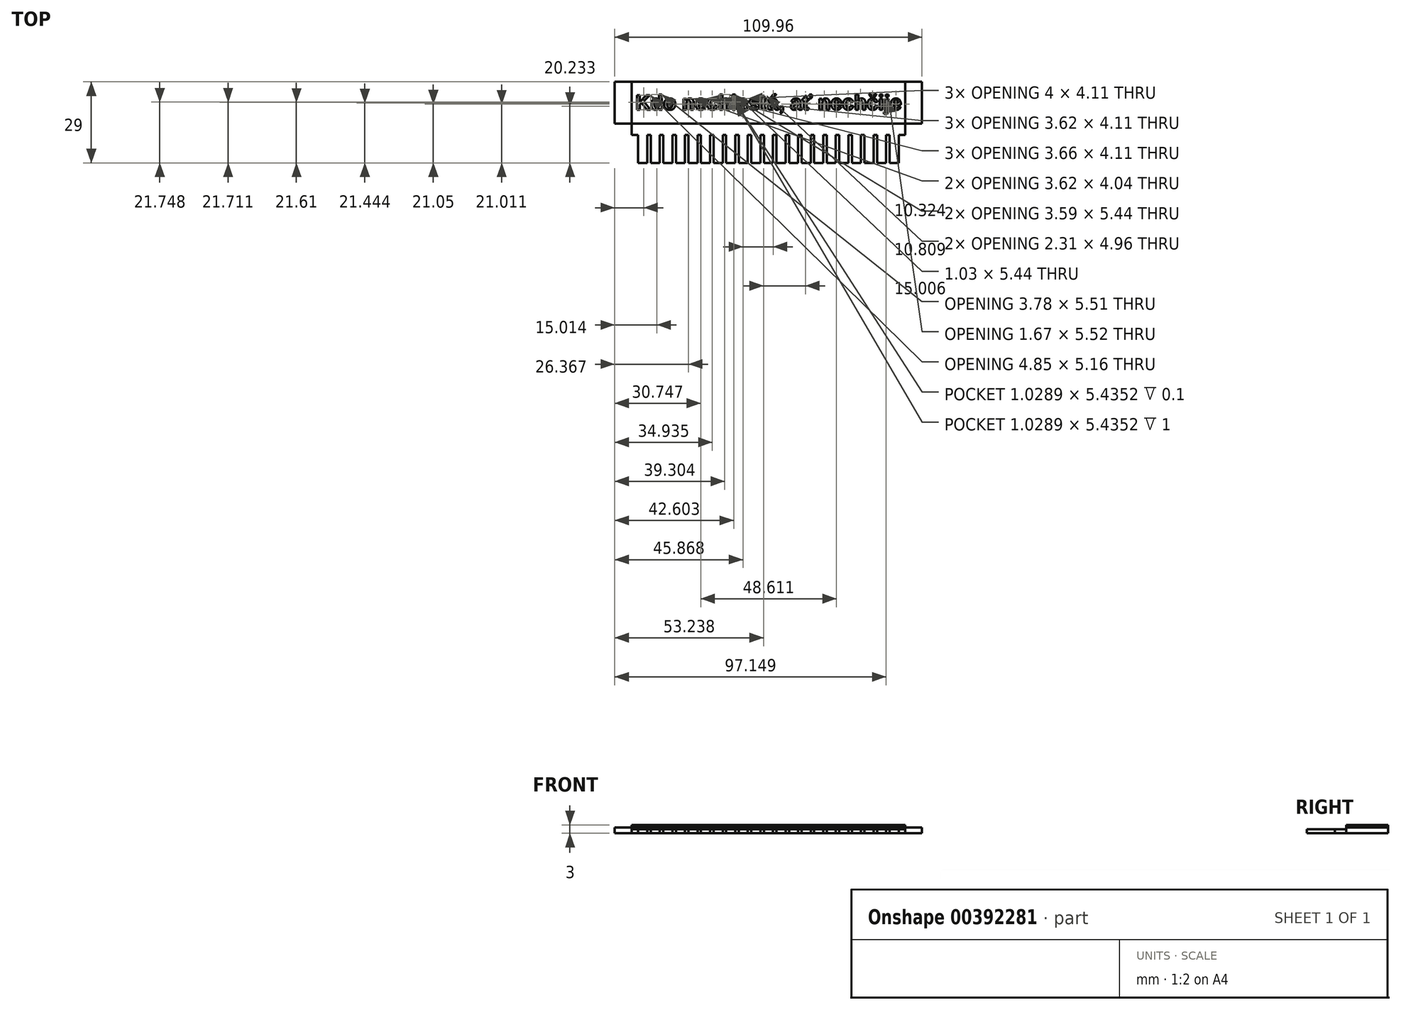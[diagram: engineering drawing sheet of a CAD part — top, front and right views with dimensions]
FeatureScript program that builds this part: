
annotation { "Feature Type Name" : "Feature", "Feature Type Description" : "" }
export const myFeature = defineFeature(function(context is Context, id is Id, definition is map)
    precondition{}
    {
        {
            var Q0;
            Q0=qCreatedBy(makeId("Top.planeOp"),FACE);
            var sketch = newSketch(context, id + "F0", { "sketchPlane" : qUnion([Q0])});
            skLineSegment(sketch, "E0.bottom", {"start": v(45.28, -13.18) * mm, "end": v(42.03, -13.18) * mm});
            skLineSegment(sketch, "E1.right", {"start": v(-47.97, -13.18) * mm, "end": v(-47.97, -3.18) * mm});
            skLineSegment(sketch, "E2.bottom", {"start": v(-47.97, -13.18) * mm, "end": v(-44.72, -13.18) * mm});
            skLineSegment(sketch, "E2.right", {"start": v(-44.72, -13.18) * mm, "end": v(-44.72, -3.18) * mm});
            skLineSegment(sketch, "E3.top", {"start": v(-44.72, -3.18) * mm, "end": v(-43.47, -3.18) * mm});
            skLineSegment(sketch, "E3.right", {"start": v(-43.47, -13.18) * mm, "end": v(-43.47, -3.18) * mm});
            skLineSegment(sketch, "E4.bottom", {"start": v(-43.47, -13.18) * mm, "end": v(-40.22, -13.18) * mm});
            skLineSegment(sketch, "E4.right", {"start": v(-40.22, -13.18) * mm, "end": v(-40.22, -3.18) * mm});
            skLineSegment(sketch, "E5.top", {"start": v(-40.22, -3.18) * mm, "end": v(-38.97, -3.18) * mm});
            skLineSegment(sketch, "E5.right", {"start": v(-38.97, -13.18) * mm, "end": v(-38.97, -3.18) * mm});
            skLineSegment(sketch, "E6.bottom", {"start": v(-38.97, -13.18) * mm, "end": v(-35.72, -13.18) * mm});
            skLineSegment(sketch, "E6.right", {"start": v(-35.72, -13.18) * mm, "end": v(-35.72, -3.18) * mm});
            skLineSegment(sketch, "E7.top", {"start": v(-35.72, -3.18) * mm, "end": v(-34.47, -3.18) * mm});
            skLineSegment(sketch, "E7.right", {"start": v(-34.47, -13.18) * mm, "end": v(-34.47, -3.18) * mm});
            skLineSegment(sketch, "E8.bottom", {"start": v(-34.47, -13.18) * mm, "end": v(-31.22, -13.18) * mm});
            skLineSegment(sketch, "E8.right", {"start": v(-31.22, -13.18) * mm, "end": v(-31.22, -3.18) * mm});
            skLineSegment(sketch, "E9.top", {"start": v(-31.22, -3.18) * mm, "end": v(-29.97, -3.18) * mm});
            skLineSegment(sketch, "E9.right", {"start": v(-29.97, -13.18) * mm, "end": v(-29.97, -3.18) * mm});
            skLineSegment(sketch, "E10.bottom", {"start": v(-29.97, -13.18) * mm, "end": v(-26.72, -13.18) * mm});
            skLineSegment(sketch, "E10.right", {"start": v(-26.72, -13.18) * mm, "end": v(-26.72, -3.18) * mm});
            skLineSegment(sketch, "E11.top", {"start": v(-26.72, -3.18) * mm, "end": v(-25.47, -3.18) * mm});
            skLineSegment(sketch, "E11.right", {"start": v(-25.47, -13.18) * mm, "end": v(-25.47, -3.18) * mm});
            skLineSegment(sketch, "E12.bottom", {"start": v(-25.47, -13.18) * mm, "end": v(-22.22, -13.18) * mm});
            skLineSegment(sketch, "E12.right", {"start": v(-22.22, -13.18) * mm, "end": v(-22.22, -3.18) * mm});
            skLineSegment(sketch, "E13.right", {"start": v(-20.97, -13.18) * mm, "end": v(-20.97, -3.18) * mm});
            skLineSegment(sketch, "E14.bottom", {"start": v(-20.97, -13.18) * mm, "end": v(-17.72, -13.18) * mm});
            skLineSegment(sketch, "E14.right", {"start": v(-17.72, -13.18) * mm, "end": v(-17.72, -3.18) * mm});
            skLineSegment(sketch, "E15.top", {"start": v(-17.72, -3.18) * mm, "end": v(-16.47, -3.18) * mm});
            skLineSegment(sketch, "E15.right", {"start": v(-16.47, -13.18) * mm, "end": v(-16.47, -3.18) * mm});
            skLineSegment(sketch, "E16.bottom", {"start": v(-16.47, -13.18) * mm, "end": v(-13.22, -13.18) * mm});
            skLineSegment(sketch, "E16.right", {"start": v(-13.22, -13.18) * mm, "end": v(-13.22, -3.18) * mm});
            skLineSegment(sketch, "E17.top", {"start": v(-13.22, -3.18) * mm, "end": v(-11.97, -3.18) * mm});
            skLineSegment(sketch, "E17.right", {"start": v(-11.97, -13.18) * mm, "end": v(-11.97, -3.18) * mm});
            skLineSegment(sketch, "E18.bottom", {"start": v(-11.97, -13.18) * mm, "end": v(-8.72, -13.18) * mm});
            skLineSegment(sketch, "E18.right", {"start": v(-8.72, -13.18) * mm, "end": v(-8.72, -3.18) * mm});
            skLineSegment(sketch, "E19.top", {"start": v(-8.72, -3.18) * mm, "end": v(-7.47, -3.18) * mm});
            skLineSegment(sketch, "E19.right", {"start": v(-7.47, -13.18) * mm, "end": v(-7.47, -3.18) * mm});
            skLineSegment(sketch, "E20.bottom", {"start": v(-7.47, -13.18) * mm, "end": v(-4.22, -13.18) * mm});
            skLineSegment(sketch, "E20.right", {"start": v(-4.22, -13.18) * mm, "end": v(-4.22, -3.18) * mm});
            skLineSegment(sketch, "E21.top", {"start": v(-4.22, -3.18) * mm, "end": v(-2.97, -3.18) * mm});
            skLineSegment(sketch, "E21.right", {"start": v(-2.97, -13.18) * mm, "end": v(-2.97, -3.18) * mm});
            skLineSegment(sketch, "E22.bottom", {"start": v(-2.97, -13.18) * mm, "end": v(0.28, -13.18) * mm});
            skLineSegment(sketch, "E22.right", {"start": v(0.28, -13.18) * mm, "end": v(0.28, -3.18) * mm});
            skLineSegment(sketch, "E23.top", {"start": v(0.28, -3.18) * mm, "end": v(1.53, -3.18) * mm});
            skLineSegment(sketch, "E23.right", {"start": v(1.53, -13.18) * mm, "end": v(1.53, -3.18) * mm});
            skLineSegment(sketch, "E24.bottom", {"start": v(1.53, -13.18) * mm, "end": v(4.78, -13.18) * mm});
            skLineSegment(sketch, "E24.right", {"start": v(4.78, -13.18) * mm, "end": v(4.78, -3.18) * mm});
            skLineSegment(sketch, "E25.top", {"start": v(4.78, -3.18) * mm, "end": v(6.03, -3.18) * mm});
            skLineSegment(sketch, "E25.right", {"start": v(6.03, -13.18) * mm, "end": v(6.03, -3.18) * mm});
            skLineSegment(sketch, "E26.bottom", {"start": v(6.03, -13.18) * mm, "end": v(9.28, -13.18) * mm});
            skLineSegment(sketch, "E26.right", {"start": v(9.28, -13.18) * mm, "end": v(9.28, -3.18) * mm});
            skLineSegment(sketch, "E27.top", {"start": v(9.28, -3.18) * mm, "end": v(10.53, -3.18) * mm});
            skLineSegment(sketch, "E27.right", {"start": v(10.53, -13.18) * mm, "end": v(10.53, -3.18) * mm});
            skLineSegment(sketch, "E28.bottom", {"start": v(10.53, -13.18) * mm, "end": v(13.78, -13.18) * mm});
            skLineSegment(sketch, "E28.right", {"start": v(13.78, -13.18) * mm, "end": v(13.78, -3.18) * mm});
            skLineSegment(sketch, "E29.top", {"start": v(13.78, -3.18) * mm, "end": v(15.03, -3.18) * mm});
            skLineSegment(sketch, "E29.right", {"start": v(15.03, -13.18) * mm, "end": v(15.03, -3.18) * mm});
            skLineSegment(sketch, "E30.bottom", {"start": v(15.03, -13.18) * mm, "end": v(18.28, -13.18) * mm});
            skLineSegment(sketch, "E30.right", {"start": v(18.28, -13.18) * mm, "end": v(18.28, -3.18) * mm});
            skLineSegment(sketch, "E31.top", {"start": v(18.28, -3.18) * mm, "end": v(19.53, -3.18) * mm});
            skLineSegment(sketch, "E31.right", {"start": v(19.53, -13.18) * mm, "end": v(19.53, -3.18) * mm});
            skLineSegment(sketch, "E32.bottom", {"start": v(19.53, -13.18) * mm, "end": v(22.78, -13.18) * mm});
            skLineSegment(sketch, "E32.right", {"start": v(22.78, -13.18) * mm, "end": v(22.78, -3.18) * mm});
            skLineSegment(sketch, "E33.top", {"start": v(22.78, -3.18) * mm, "end": v(24.03, -3.18) * mm});
            skLineSegment(sketch, "E33.right", {"start": v(24.03, -13.18) * mm, "end": v(24.03, -3.18) * mm});
            skLineSegment(sketch, "E34.bottom", {"start": v(24.03, -13.18) * mm, "end": v(27.28, -13.18) * mm});
            skLineSegment(sketch, "E34.right", {"start": v(27.28, -13.18) * mm, "end": v(27.28, -3.18) * mm});
            skLineSegment(sketch, "E35.top", {"start": v(27.28, -3.18) * mm, "end": v(28.53, -3.18) * mm});
            skLineSegment(sketch, "E35.right", {"start": v(28.53, -13.18) * mm, "end": v(28.53, -3.18) * mm});
            skLineSegment(sketch, "E36.bottom", {"start": v(28.53, -13.18) * mm, "end": v(31.78, -13.18) * mm});
            skLineSegment(sketch, "E36.right", {"start": v(31.78, -13.18) * mm, "end": v(31.78, -3.18) * mm});
            skLineSegment(sketch, "E37.top", {"start": v(31.78, -3.18) * mm, "end": v(33.03, -3.18) * mm});
            skLineSegment(sketch, "E37.right", {"start": v(33.03, -13.18) * mm, "end": v(33.03, -3.18) * mm});
            skLineSegment(sketch, "E38.bottom", {"start": v(33.03, -13.18) * mm, "end": v(36.28, -13.18) * mm});
            skLineSegment(sketch, "E38.right", {"start": v(36.28, -13.18) * mm, "end": v(36.28, -3.18) * mm});
            skLineSegment(sketch, "E39.top", {"start": v(36.28, -3.18) * mm, "end": v(37.53, -3.18) * mm});
            skLineSegment(sketch, "E39.right", {"start": v(37.53, -13.18) * mm, "end": v(37.53, -3.18) * mm});
            skLineSegment(sketch, "E40.bottom", {"start": v(37.53, -13.18) * mm, "end": v(40.78, -13.18) * mm});
            skLineSegment(sketch, "E40.right", {"start": v(40.78, -13.18) * mm, "end": v(40.78, -3.18) * mm});
            skLineSegment(sketch, "E41.bottom", {"start": v(42.03, -13.18) * mm, "end": v(45.28, -13.18) * mm});
            skLineSegment(sketch, "E41.left", {"start": v(42.03, -13.18) * mm, "end": v(42.03, -3.18) * mm});
            skLineSegment(sketch, "E42.left", {"start": v(45.28, -13.18) * mm, "end": v(45.28, -3.18) * mm});
            skLineSegment(sketch, "E43.trimOffspring", {"start": v(36.28, -13.18) * mm, "end": v(33.03, -13.18) * mm});
            skLineSegment(sketch, "E44.trimOffspring", {"start": v(31.78, -13.18) * mm, "end": v(28.53, -13.18) * mm});
            skLineSegment(sketch, "E45.trimOffspring", {"start": v(27.28, -13.18) * mm, "end": v(24.03, -13.18) * mm});
            skLineSegment(sketch, "E46.trimOffspring", {"start": v(22.78, -13.18) * mm, "end": v(19.53, -13.18) * mm});
            skLineSegment(sketch, "E47.trimOffspring", {"start": v(18.28, -13.18) * mm, "end": v(15.03, -13.18) * mm});
            skLineSegment(sketch, "E48.trimOffspring", {"start": v(13.78, -13.18) * mm, "end": v(10.53, -13.18) * mm});
            skLineSegment(sketch, "E49.trimOffspring", {"start": v(9.28, -13.18) * mm, "end": v(6.03, -13.18) * mm});
            skLineSegment(sketch, "E50.trimOffspring", {"start": v(4.78, -13.18) * mm, "end": v(1.53, -13.18) * mm});
            skLineSegment(sketch, "E51.trimOffspring", {"start": v(0.28, -13.18) * mm, "end": v(-2.97, -13.18) * mm});
            skLineSegment(sketch, "E52.trimOffspring", {"start": v(-4.22, -13.18) * mm, "end": v(-7.47, -13.18) * mm});
            skLineSegment(sketch, "E53.trimOffspring", {"start": v(-8.72, -13.18) * mm, "end": v(-11.97, -13.18) * mm});
            skLineSegment(sketch, "E54.trimOffspring", {"start": v(-13.22, -13.18) * mm, "end": v(-16.47, -13.18) * mm});
            skLineSegment(sketch, "E55.trimOffspring", {"start": v(-22.22, -13.18) * mm, "end": v(-25.47, -13.18) * mm});
            skLineSegment(sketch, "E56.trimOffspring", {"start": v(-26.72, -13.18) * mm, "end": v(-29.97, -13.18) * mm});
            skLineSegment(sketch, "E57.trimOffspring", {"start": v(-31.22, -13.18) * mm, "end": v(-34.47, -13.18) * mm});
            skLineSegment(sketch, "E58.trimOffspring", {"start": v(-35.72, -13.18) * mm, "end": v(-38.97, -13.18) * mm});
            skLineSegment(sketch, "E59.trimOffspring", {"start": v(-40.22, -13.18) * mm, "end": v(-43.47, -13.18) * mm});
            skLineSegment(sketch, "E60.trimOffspring", {"start": v(-44.72, -13.18) * mm, "end": v(-47.97, -13.18) * mm});
            skLineSegment(sketch, "E61", {"start": v(-47.97, -3.18) * mm, "end": v(-50.34, -3.18) * mm});
            skLineSegment(sketch, "E62", {"start": v(47.62, -3.18) * mm, "end": v(47.62, 15.82) * mm});
            skLineSegment(sketch, "E63", {"start": v(-50.34, -3.18) * mm, "end": v(-50.34, 15.82) * mm});
            skLineSegment(sketch, "E64", {"start": v(47.62, 0.82) * mm, "end": v(53.62, 0.82) * mm});
            skLineSegment(sketch, "E65", {"start": v(53.62, 0.82) * mm, "end": v(53.62, 15.82) * mm});
            skLineSegment(sketch, "E66", {"start": v(-50.34, 0.82) * mm, "end": v(-56.34, 0.82) * mm});
            skLineSegment(sketch, "E67", {"start": v(-22.22, -3.18) * mm, "end": v(-20.97, -3.18) * mm});
            skLineSegment(sketch, "E68", {"start": v(40.78, -3.18) * mm, "end": v(42.03, -3.18) * mm});
            skLineSegment(sketch, "E69", {"start": v(47.62, -3.18) * mm, "end": v(45.28, -3.18) * mm});
            skLineSegment(sketch, "E70", {"start": v(-56.34, 0.82) * mm, "end": v(-56.34, 15.82) * mm});
            skLineSegment(sketch, "E71", {"start": v(-56.34, 15.82) * mm, "end": v(53.62, 15.82) * mm});
            skLineSegment(sketch, "E72", {"start": v(-50.34, 0.82) * mm, "end": v(47.62, 0.82) * mm});
            skSolve(sketch);
        }
        {
            var Q0;
            Q0=makeQuery(id+"F0.imprint","IMPRINT",FACE,{"disambiguationData":[TD([[makeQuery(id+"F0.imprint","IMPRINT",EDGE,{"derivedFrom":sQuery(id+"F0.wireOp",EDGE,"E1.right")}),-1.0]])]});
            extrude(context, id + "F1", {"entities" : qUnion([Q0]), "depth" : 1.5 * mm});
        }
        {
            var Q0;
            {var subQ3=sQuery(id+"F0.wireOp",EDGE,"E66");Q0=makeQuery(id+"F0.imprint","IMPRINT",FACE,{"disambiguationData":[TD([[makeQuery(id+"F0.imprint","IMPRINT",EDGE,{"derivedFrom":subQ3}),-1.0]])]});}
            var Q1;
            {var subQ3=sQuery(id+"F0.wireOp",EDGE,"E64");Q1=makeQuery(id+"F0.imprint","IMPRINT",FACE,{"disambiguationData":[TD([[makeQuery(id+"F0.imprint","IMPRINT",EDGE,{"derivedFrom":subQ3}),1.0]])]});}
            var Q2;
            {var subQ3=sQuery(id+"F0.wireOp",EDGE,"E72");Q2=makeQuery(id+"F0.imprint","IMPRINT",FACE,{"disambiguationData":[TD([[makeQuery(id+"F0.imprint","IMPRINT",EDGE,{"derivedFrom":subQ3}),1.0]])]});}
            extrude(context, id + "F2", {"entities" : qUnion([Q0, Q1, Q2]), "depth" : 2.1 * mm});
        }
        {
            var Q0;
            {var subQ3=sQuery(id+"F0.wireOp",EDGE,"E72");Q0=makeQuery(id+"F0.imprint","IMPRINT",FACE,{"disambiguationData":[TD([[makeQuery(id+"F0.imprint","IMPRINT",EDGE,{"derivedFrom":subQ3}),1.0]])]});}
            extrude(context, id + "F3", {"entities" : qUnion([Q0]), "depth" : 3 * mm});
        }
        {
            var Q0;
            Q0=makeQuery(id+"F3.opExtrude","CAP_FACE",FACE,{"disambiguationData":[OSD([sQuery(id+"F0.wireOp",EDGE,"E62"),sQuery(id+"F0.wireOp",EDGE,"E63"),sQuery(id+"F0.wireOp",EDGE,"E71"),sQuery(id+"F0.wireOp",EDGE,"E72")])],"isStart":false});
            var sketch = newSketch(context, id + "F4", { "sketchPlane" : qUnion([Q0])});
            skText(sketch, "E73", { "text": "Kdo nechlastá, ať nechčije", "fontName": "Arimo-Bold.ttf"});
            const initialGuessF4  = {"E73": [-0.04894, 0.00585, 1, 0, 0.0054]};
            skSetInitialGuess(sketch, initialGuessF4);
            skSolve(sketch);
        }
        {
            var Q0;
            Q0 = qSketchRegion(id + "F4", true);
            extrude(context, id + "F5", {"entities" : qUnion([Q0]), "operationType" : NewBodyOperationType.REMOVE, "oppositeDirection" : true, "depth" : 1 * mm});
        }
    });
